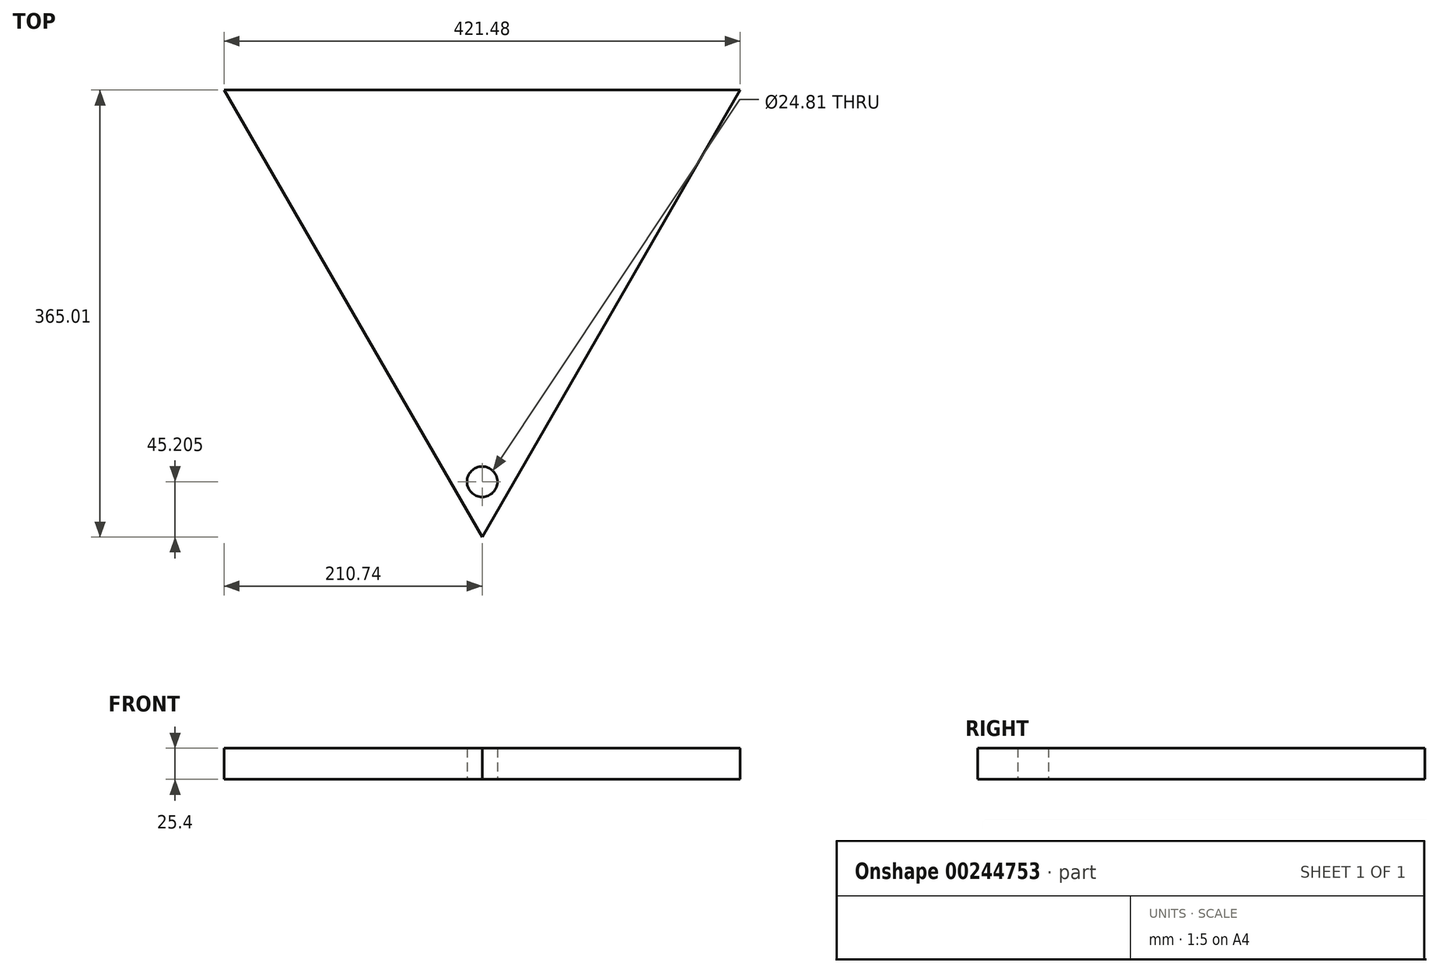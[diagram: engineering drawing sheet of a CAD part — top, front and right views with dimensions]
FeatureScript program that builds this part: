
annotation { "Feature Type Name" : "Feature", "Feature Type Description" : "" }
export const myFeature = defineFeature(function(context is Context, id is Id, definition is map)
    precondition{}
    {
        {
            var Q0;
            Q0=qCreatedBy(makeId("Top.planeOp"),FACE);
            var sketch = newSketch(context, id + "F0", { "sketchPlane" : qUnion([Q0])});
            skCircle(sketch, "E0.cCircle", {"center": v(0, 0) * mm, "radius": 121.67 * mm, "construction": true});
            skLineSegment(sketch, "E0.0", {"start": v(-210.74, 121.67) * mm, "end": v(210.74, 121.67) * mm});
            skLineSegment(sketch, "E0.1", {"start": v(210.74, 121.67) * mm, "end": v(0, -243.34) * mm});
            skLineSegment(sketch, "E0.2", {"start": v(0, -243.34) * mm, "end": v(-210.74, 121.67) * mm});
            skPoint(sketch, "E0.0.midPoint", {"position": v(0, 121.67) * mm});
            skSolve(sketch);
        }
        {
            var Q0;
            Q0 = qSketchRegion(id + "F0", true);
            extrude(context, id + "F1", {"entities" : qUnion([Q0]), "depth" : 25.4 * mm});
        }
        {
            var Q0;
            Q0=makeQuery(id+"F1.opExtrude","CAP_FACE",FACE,{"disambiguationData":[OSD([sQuery(id+"F0.wireOp",EDGE,"E0.0"),sQuery(id+"F0.wireOp",EDGE,"E0.1"),sQuery(id+"F0.wireOp",EDGE,"E0.2")])],"isStart":true});
            var sketch = newSketch(context, id + "F2", { "sketchPlane" : qUnion([Q0])});
            skCircle(sketch, "E1", {"center": v(0, 198.14) * mm, "radius": 12.4 * mm});
            skSolve(sketch);
        }
        {
            var Q0;
            Q0 = qSketchRegion(id + "F2", true);
            extrude(context, id + "F3", {"entities" : qUnion([Q0]), "operationType" : NewBodyOperationType.REMOVE, "oppositeDirection" : true, "depth" : 25.4 * mm});
        }
    });
